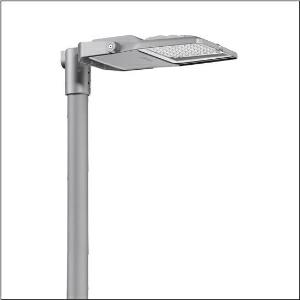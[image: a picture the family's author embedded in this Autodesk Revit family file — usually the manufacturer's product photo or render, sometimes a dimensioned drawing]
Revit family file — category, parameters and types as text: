
# Revit family: floodlight_fl_21_iq_mini___pl43_5xa7772d4a3a_0702
name_source: partatom
category: Lighting Fixtures
units: mm (PartAtom-declared; Revit-internal decimal feet)

## family parameters
Cut with Voids When Loaded = No
Host = Face
Light Source = No
Part Type = Normal
Room Calculation Point = No
Round Connector Dimension = Use Diameter
Shared = No

## types (1)
- --- (1 x LED, 19090 lm, 143 W, 4000K)
    Apparent Load = 143 VA
    CIE Flux Codes = 27 78 99 100 100
    Color Rendering = 70
    Color Temperature = 4000K
    Default Elevation = 1800 mm
    Description = Floodlight FL 21 iQ mini, floodlight, primary light control with lens, of PMMA, primary optical cover: protective disc, of toughened safety glass, transparent, light distribution: PL43, light emission: direct distribution, installation type: surface-mounted, LED, High Power LED, rated luminous flux: 19.090lm, luminous efficacy: 134lm/W, light colour: 740, colour temperature: 4000K, control: Auto-Match, Temp-Guard, Night-Set, Smart-Wire, Desk-Remote (wireless, voltage-free reading and setting of iQ features in the workshop via application-optimized NFC function/RFID function), optimised constant luminous flux control (CLO 2.0), Light-Fading, Lumen-Switch, with terminal, 6-pole, mains connection: 220..240V, AC, 50/60Hz, start of lifetime: 143W, end of service life: 152W, reduction: 61W, luminaire housing, of diecast aluminium, powder-coated, Siteco® metallic grey (DB 702S), corrosivity category C5 mid according to DIN EN ISO 12944, sealing non-destructively replaceable, please order mast flange separately, mast bracket, of steel, galvanised, powder-coated, protection rating (complete): IP66, insulation class (complete): insulation class II (safety insulation), certification: CE, ENEC, VDE, protection symbol: D, impact resistance: IK08, permissible operating ambient temperature: -40..+40°C, permissible operating ambient temperature for outdoor applications: -40..+50°C, standard: DIN EN 12944, LABS conformity tested according to VDMA 24364:2018-05, packaging unit: 1 piece

Light Distribution: PL43
    Height = 70 mm
    Lamp = 1 x LED
    Lamp Light Flux = 19090 lm
    Lamp Power = 143 W
    Lamp count = 1
    Length = 485 mm
    Luminous efficacy = 133 lm/W
    Manufacturer = Siteco
    ModVariant = No
    Model = 5XA7772D4A3A
    Number of Poles = 1
    OnlyDefault = Yes
    Power Factor = 1
    Product Name = Floodlight FL 21 iQ mini | PL43
    Product group = floodlight | pylon annexe
    ProductGroupID = 6200
    Protection Class = Protection class II
    Protection Degree = IP 66
    RLX_Detail_Level = 1
    RLX_Emergency_Light_Flux = 0 lm
    RLX_Emergency_Type = 0
    RLX_Emergency_Type_DB = No
    RlxData = <blob elided: 101581 chars, md5=43162146>
    Socket = socket
    Standby Power = 0 W
    System Light Flux = 19090 lm
    System Power = 143 W
    Type Comments = factory setting: luminous flux: 100 % | dim-lin: 254 | 730 mA
    Type Image = l_1007125.jpg
    URL = http://relux.com
    VarID = @adj_131807
    Voltage = 0 V
    Weight = 0.00 kg
    Width = 337 mm

## geometry (parser evidence)
native form markers: Blend x4, Sweep x10
no freeform markers — native parametric forms only
